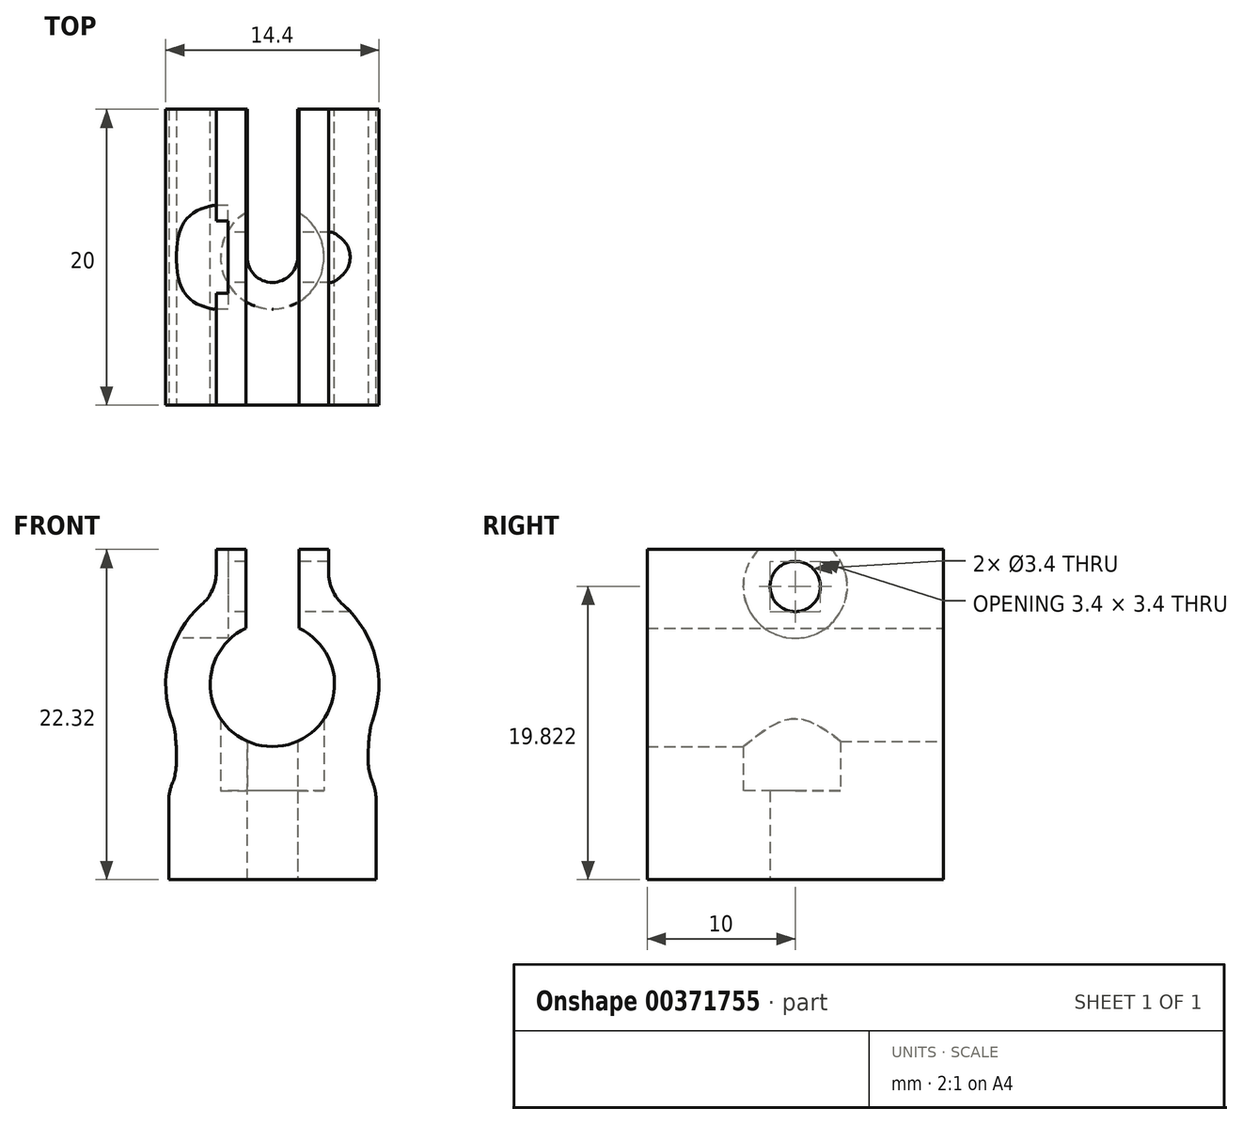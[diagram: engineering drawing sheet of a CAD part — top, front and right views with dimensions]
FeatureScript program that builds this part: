
annotation { "Feature Type Name" : "Feature", "Feature Type Description" : "" }
export const myFeature = defineFeature(function(context is Context, id is Id, definition is map)
    precondition{}
    {
        {
            var Q0;
            Q0=qCreatedBy(makeId("Front.planeOp"),FACE);
            var sketch = newSketch(context, id + "F0", { "sketchPlane" : qUnion([Q0])});
            skArc(sketch, "E0", {"start": v(-1.79, 3.8) * mm, "mid": v(0, -4.2) * mm, "end": v(1.79, 3.8) * mm});
            skArc(sketch, "E1", {"start": v(-3.79, 6.12) * mm, "mid": v(-6.86, 2.19) * mm, "end": v(-6.64, -2.8) * mm});
            skLineSegment(sketch, "E2", {"start": v(3.79, 9.12) * mm, "end": v(3.79, 6.12) * mm});
            skLineSegment(sketch, "E3", {"start": v(-1.79, 9.12) * mm, "end": v(-1.79, 3.8) * mm});
            skLineSegment(sketch, "E4", {"start": v(1.79, 9.12) * mm, "end": v(1.79, 3.8) * mm});
            skLineSegment(sketch, "E5", {"start": v(-1.79, 9.12) * mm, "end": v(-3.79, 9.12) * mm});
            skLineSegment(sketch, "E6", {"start": v(-3.79, 6.12) * mm, "end": v(-3.79, 9.12) * mm});
            skLineSegment(sketch, "E7", {"start": v(1.79, 9.12) * mm, "end": v(3.79, 9.12) * mm});
            skLineSegment(sketch, "E8", {"start": v(-7, -7.2) * mm, "end": v(-7, -13.2) * mm});
            skLineSegment(sketch, "E9", {"start": v(-7, -13.2) * mm, "end": v(7, -13.2) * mm});
            skLineSegment(sketch, "E10", {"start": v(7, -7.2) * mm, "end": v(7, -13.2) * mm});
            skPoint(sketch, "E11.orphan", {"position": v(9.08, -13.2) * mm});
            skFitSpline(sketch, "E12", {"points": [v(-7, -7.2) * mm, v(-6.5, -5.54) * mm, v(-6.64, -2.8) * mm, v(-6.64, -2.77) * mm], "startDerivative": vector(1.57, 3.06) * mm, "endDerivative": vector(-0.17, 0.18) * mm});
            skFitSpline(sketch, "E13", {"points": [v(7, -7.2) * mm, v(6.5, -5.54) * mm, v(6.64, -2.8) * mm], "startDerivative": vector(-1.44, 3.48) * mm, "endDerivative": vector(0.64, 5.26) * mm});
            skArc(sketch, "E14.trimOffspring", {"start": v(6.64, -2.8) * mm, "mid": v(6.86, 2.19) * mm, "end": v(3.79, 6.12) * mm});
            skLineSegment(sketch, "E15", {"start": v(-1.7, -4.2) * mm, "end": v(-1.7, -3.84) * mm});
            skLineSegment(sketch, "E16", {"start": v(-1.7, -4.2) * mm, "end": v(-1.7, -13.2) * mm});
            skLineSegment(sketch, "E17", {"start": v(1.7, -4.2) * mm, "end": v(1.7, -3.84) * mm});
            skLineSegment(sketch, "E18", {"start": v(1.7, -4.2) * mm, "end": v(1.7, -13.2) * mm});
            skPoint(sketch, "E19.start.orphan", {"position": v(0, -4.2) * mm});
            skLineSegment(sketch, "E20", {"start": v(0, -4.2) * mm, "end": v(1.7, -4.2) * mm, "construction": true});
            skLineSegment(sketch, "E21", {"start": v(0, -4.2) * mm, "end": v(-1.7, -4.2) * mm, "construction": true});
            skSolve(sketch);
        }
        {
            var Q0;
            Q0 = qSketchRegion(id + "F0", true);
            extrude(context, id + "F1", {"entities" : qUnion([Q0]), "depth" : 20 * mm, "offsetDistance" : 25 * mm});
        }
        {
            var Q0;
            Q0=makeQuery(id+"F1.opExtrude","SWEPT_FACE",FACE,{"disambiguationData":[OSD([sQuery(id+"F0.wireOp",EDGE,"E8")])]});
            var sketch = newSketch(context, id + "F2", { "sketchPlane" : qUnion([Q0])});
            skLineSegment(sketch, "E22", {"start": v(10, -13.2) * mm, "end": v(10, 6.62) * mm, "construction": true});
            skCircle(sketch, "E23", {"center": v(10, 6.62) * mm, "radius": 1.7 * mm});
            skCircle(sketch, "E24", {"center": v(10, 6.62) * mm, "radius": 3.5 * mm});
            skSolve(sketch);
        }
        {
            var Q0;
            Q0=makeQuery(id+"F2.imprint","IMPRINT",FACE,{"disambiguationData":[TD([[makeQuery(id+"F2.imprint","IMPRINT",EDGE,{"derivedFrom":sQuery(id+"F2.wireOp",EDGE,"E23")}),-1.0]])]});
            extrude(context, id + "F3", {"entities" : qUnion([Q0]), "operationType" : NewBodyOperationType.REMOVE, "oppositeDirection" : true, "depth" : 4 * mm});
        }
        {
            var Q0;
            Q0=makeQuery(id+"F2.imprint","IMPRINT",FACE,{"disambiguationData":[TD([[makeQuery(id+"F2.imprint","IMPRINT",EDGE,{"derivedFrom":sQuery(id+"F2.wireOp",EDGE,"E23")}),1.0]])]});
            extrude(context, id + "F4", {"entities" : qUnion([Q0]), "operationType" : NewBodyOperationType.REMOVE, "oppositeDirection" : true, "depth" : 25 * mm});
        }
        {
            var Q0;
            Q0=makeQuery(id+"F1.opExtrude","SWEPT_EDGE",EDGE,{"disambiguationData":[OSD([sQuery(id+"F0.wireOp",EDGE,"E1"),sQuery(id+"F0.wireOp",EDGE,"E12")])]});
            var Q1;
            Q1=makeQuery(id+"F1.opExtrude","SWEPT_EDGE",EDGE,{"disambiguationData":[OSD([sQuery(id+"F0.wireOp",EDGE,"E13"),sQuery(id+"F0.wireOp",EDGE,"E14.trimOffspring")])]});
            var Q2;
            Q2=makeQuery(id+"F1.opExtrude","SWEPT_EDGE",EDGE,{"disambiguationData":[OSD([sQuery(id+"F0.wireOp",EDGE,"E8"),sQuery(id+"F0.wireOp",EDGE,"E12")])]});
            var Q3;
            Q3=makeQuery(id+"F1.opExtrude","SWEPT_EDGE",EDGE,{"disambiguationData":[OSD([sQuery(id+"F0.wireOp",EDGE,"E10"),sQuery(id+"F0.wireOp",EDGE,"E13")])]});
            var Q4;
            {var subQ0=sQuery(id+"F0.wireOp",EDGE,"E14.trimOffspring");var subQ1=sQuery(id+"F0.wireOp",EDGE,"E2");Q4=makeQuery(id+"F4.boolean.opBoolean","SPLIT",EDGE,{"disambiguationData":[TD([makeQuery(id+"F1.opExtrude","CAP_FACE",FACE,{"disambiguationData":[OSD([sQuery(id+"F0.wireOp",EDGE,"E0"),sQuery(id+"F0.wireOp",EDGE,"E1"),subQ1,sQuery(id+"F0.wireOp",EDGE,"E3"),sQuery(id+"F0.wireOp",EDGE,"E4"),sQuery(id+"F0.wireOp",EDGE,"E5"),sQuery(id+"F0.wireOp",EDGE,"E6"),sQuery(id+"F0.wireOp",EDGE,"E7"),sQuery(id+"F0.wireOp",EDGE,"E8"),sQuery(id+"F0.wireOp",EDGE,"E9"),sQuery(id+"F0.wireOp",EDGE,"E10"),sQuery(id+"F0.wireOp",EDGE,"E12"),sQuery(id+"F0.wireOp",EDGE,"E13"),subQ0])],"isStart":false})])],"derivedFrom":makeQuery(id+"F1.opExtrude","SWEPT_EDGE",EDGE,{"disambiguationData":[OSD([subQ1,subQ0])]})});}
            var Q5;
            {var subQ0=sQuery(id+"F0.wireOp",EDGE,"E14.trimOffspring");var subQ1=sQuery(id+"F0.wireOp",EDGE,"E2");Q5=makeQuery(id+"F4.boolean.opBoolean","SPLIT",EDGE,{"disambiguationData":[TD([makeQuery(id+"F1.opExtrude","CAP_FACE",FACE,{"disambiguationData":[OSD([sQuery(id+"F0.wireOp",EDGE,"E0"),sQuery(id+"F0.wireOp",EDGE,"E1"),subQ1,sQuery(id+"F0.wireOp",EDGE,"E3"),sQuery(id+"F0.wireOp",EDGE,"E4"),sQuery(id+"F0.wireOp",EDGE,"E5"),sQuery(id+"F0.wireOp",EDGE,"E6"),sQuery(id+"F0.wireOp",EDGE,"E7"),sQuery(id+"F0.wireOp",EDGE,"E8"),sQuery(id+"F0.wireOp",EDGE,"E9"),sQuery(id+"F0.wireOp",EDGE,"E10"),sQuery(id+"F0.wireOp",EDGE,"E12"),sQuery(id+"F0.wireOp",EDGE,"E13"),subQ0])],"isStart":true})])],"derivedFrom":makeQuery(id+"F1.opExtrude","SWEPT_EDGE",EDGE,{"disambiguationData":[OSD([subQ1,subQ0])]})});}
            var Q6;
            {var subQ0=sQuery(id+"F0.wireOp",EDGE,"E6");var subQ1=sQuery(id+"F0.wireOp",EDGE,"E1");Q6=makeQuery(id+"F3.boolean.opBoolean","SPLIT",EDGE,{"disambiguationData":[TD([makeQuery(id+"F1.opExtrude","CAP_FACE",FACE,{"disambiguationData":[OSD([sQuery(id+"F0.wireOp",EDGE,"E0"),subQ1,sQuery(id+"F0.wireOp",EDGE,"E2"),sQuery(id+"F0.wireOp",EDGE,"E3"),sQuery(id+"F0.wireOp",EDGE,"E4"),sQuery(id+"F0.wireOp",EDGE,"E5"),subQ0,sQuery(id+"F0.wireOp",EDGE,"E7"),sQuery(id+"F0.wireOp",EDGE,"E8"),sQuery(id+"F0.wireOp",EDGE,"E9"),sQuery(id+"F0.wireOp",EDGE,"E10"),sQuery(id+"F0.wireOp",EDGE,"E12"),sQuery(id+"F0.wireOp",EDGE,"E13"),sQuery(id+"F0.wireOp",EDGE,"E14.trimOffspring")])],"isStart":true})])],"derivedFrom":makeQuery(id+"F1.opExtrude","SWEPT_EDGE",EDGE,{"disambiguationData":[OSD([subQ1,subQ0])]})});}
            var Q7;
            {var subQ0=sQuery(id+"F0.wireOp",EDGE,"E6");var subQ1=sQuery(id+"F0.wireOp",EDGE,"E1");Q7=makeQuery(id+"F3.boolean.opBoolean","SPLIT",EDGE,{"disambiguationData":[TD([makeQuery(id+"F1.opExtrude","CAP_FACE",FACE,{"disambiguationData":[OSD([sQuery(id+"F0.wireOp",EDGE,"E0"),subQ1,sQuery(id+"F0.wireOp",EDGE,"E2"),sQuery(id+"F0.wireOp",EDGE,"E3"),sQuery(id+"F0.wireOp",EDGE,"E4"),sQuery(id+"F0.wireOp",EDGE,"E5"),subQ0,sQuery(id+"F0.wireOp",EDGE,"E7"),sQuery(id+"F0.wireOp",EDGE,"E8"),sQuery(id+"F0.wireOp",EDGE,"E9"),sQuery(id+"F0.wireOp",EDGE,"E10"),sQuery(id+"F0.wireOp",EDGE,"E12"),sQuery(id+"F0.wireOp",EDGE,"E13"),sQuery(id+"F0.wireOp",EDGE,"E14.trimOffspring")])],"isStart":false})])],"derivedFrom":makeQuery(id+"F1.opExtrude","SWEPT_EDGE",EDGE,{"disambiguationData":[OSD([subQ1,subQ0])]})});}
            fillet(context, id + "F5", {"entities" : qUnion([Q0, Q1, Q2, Q3, Q4, Q5, Q6, Q7]), "radius" : 3 * mm, "tangentPropagation" : true, "allowEdgeOverflow" : false});
        }
        {
            var Q0;
            Q0=makeQuery(id+"F1.opExtrude","SWEPT_FACE",FACE,{"disambiguationData":[OSD([sQuery(id+"F0.wireOp",EDGE,"E9")])]});
            var sketch = newSketch(context, id + "F6", { "sketchPlane" : qUnion([Q0])});
            skLineSegment(sketch, "E25", {"start": v(-7, 10) * mm, "end": v(0, 10) * mm, "construction": true});
            skCircle(sketch, "E26", {"center": v(0, 10) * mm, "radius": 1.7 * mm});
            skCircle(sketch, "E27", {"center": v(0, 10) * mm, "radius": 3.5 * mm});
            skSolve(sketch);
        }
        {
            var Q0;
            Q0=makeQuery(id+"F6.imprint","IMPRINT",FACE,{"disambiguationData":[TD([[makeQuery(id+"F6.imprint","IMPRINT",EDGE,{"derivedFrom":sQuery(id+"F6.wireOp",EDGE,"E26")}),-1.0]])]});
            extrude(context, id + "F7", {"entities" : qUnion([Q0]), "operationType" : NewBodyOperationType.REMOVE, "oppositeDirection" : true, "depth" : 12 * mm});
        }
        {
            var Q0;
            Q0=makeQuery(id+"F7.boolean.opBoolean","SPLIT",FACE,{"disambiguationData":[TD([makeQuery(id+"F7.opExtrude","SWEPT_FACE",FACE,{"disambiguationData":[OSD([sQuery(id+"F6.wireOp",EDGE,"E26")])]})])],"derivedFrom":makeQuery(id+"F1.opExtrude","SWEPT_FACE",FACE,{"disambiguationData":[OSD([sQuery(id+"F0.wireOp",EDGE,"E9")])]})});
            extrude(context, id + "F8", {"entities" : qUnion([Q0]), "operationType" : NewBodyOperationType.REMOVE, "oppositeDirection" : true, "depth" : 12 * mm});
        }
        {
            var Q0;
            Q0=makeQuery(id+"F6.imprint","IMPRINT",FACE,{"disambiguationData":[TD([[makeQuery(id+"F6.imprint","IMPRINT",EDGE,{"derivedFrom":sQuery(id+"F6.wireOp",EDGE,"E26")}),-1.0]])]});
            extrude(context, id + "F9", {"entities" : qUnion([Q0]), "operationType" : NewBodyOperationType.ADD, "oppositeDirection" : true, "depth" : 6 * mm});
        }
        {
            var Q0;
            {var subQ0=sQuery(id+"F0.wireOp",EDGE,"E15");Q0=makeQuery(id+"F0.imprint","IMPRINT",FACE,{"disambiguationData":[TD([[makeQuery(id+"F0.imprint","IMPRINT",EDGE,{"derivedFrom":subQ0}),-1.0]])]});}
            extrude(context, id + "F10", {"entities" : qUnion([Q0]), "operationType" : NewBodyOperationType.REMOVE, "depth" : 10 * mm});
        }
    });
